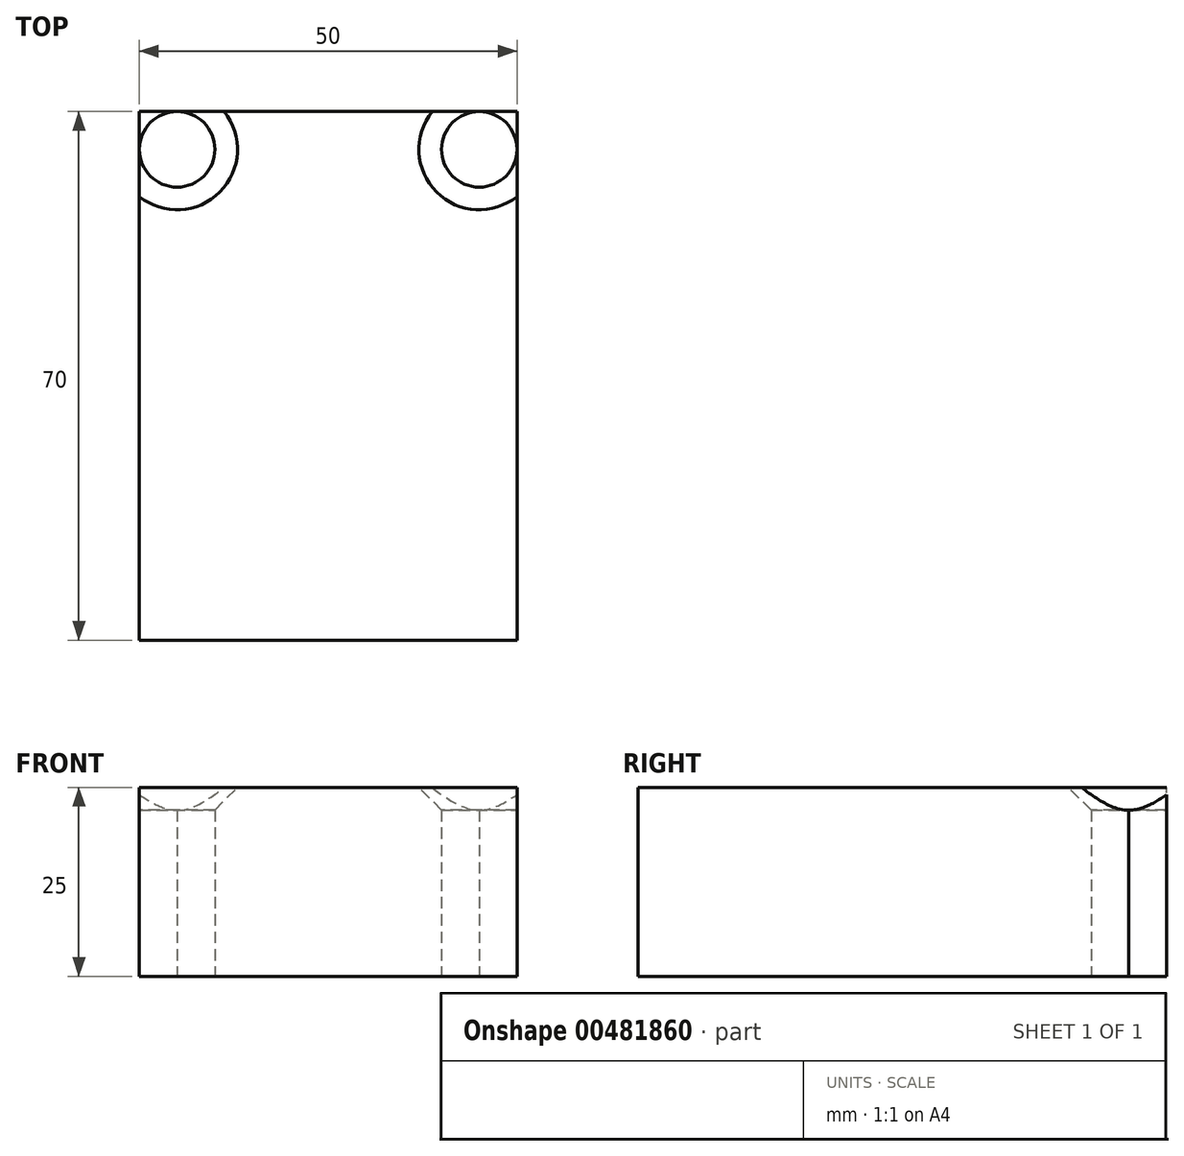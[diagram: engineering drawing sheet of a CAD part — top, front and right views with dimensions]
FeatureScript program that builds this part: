
annotation { "Feature Type Name" : "Feature", "Feature Type Description" : "" }
export const myFeature = defineFeature(function(context is Context, id is Id, definition is map)
    precondition{}
    {
        {
            var Q0;
            Q0=qCreatedBy(makeId("Top.planeOp"),FACE);
            var sketch = newSketch(context, id + "F0", { "sketchPlane" : qUnion([Q0])});
            skLineSegment(sketch, "E0.bottom", {"start": v(-25, 35) * mm, "end": v(25, 35) * mm});
            skLineSegment(sketch, "E0.top", {"start": v(-25, -35) * mm, "end": v(25, -35) * mm});
            skLineSegment(sketch, "E0.left", {"start": v(-25, 35) * mm, "end": v(-25, -35) * mm});
            skLineSegment(sketch, "E0.right", {"start": v(25, 35) * mm, "end": v(25, -35) * mm});
            skPoint(sketch, "E0.middle", {"position": v(0, 0) * mm});
            skCircle(sketch, "E1", {"center": v(-20, 30) * mm, "radius": 5 * mm});
            skCircle(sketch, "E2", {"center": v(20, 30) * mm, "radius": 5 * mm});
            skSolve(sketch);
        }
        {
            var Q0;
            Q0 = qSketchRegion(id + "F0", true);
            extrude(context, id + "F1", {"entities" : qUnion([Q0]), "depth" : 25 * mm});
        }
        {
            var Q0;
            {var subQ0=sQuery(id+"F0.wireOp",EDGE,"E1");var subQ1=makeQuery(id+"F0.imprint","INTERSECT",VERTEX,{"derivedFrom":[sQuery(id+"F0.wireOp",EDGE,"E0.bottom"),subQ0]});Q0=makeQuery(id+"F0.imprint","IMPRINT",FACE,{"disambiguationData":[TD([[makeQuery(id+"F0.imprint","IMPRINT",EDGE,{"disambiguationData":[TD([[subQ1,-1.0]])],"derivedFrom":subQ0}),1.0]])]});}
            var Q1;
            {var subQ0=sQuery(id+"F0.wireOp",EDGE,"E2");var subQ1=makeQuery(id+"F0.imprint","INTERSECT",VERTEX,{"derivedFrom":[sQuery(id+"F0.wireOp",EDGE,"E0.bottom"),subQ0]});Q1=makeQuery(id+"F0.imprint","IMPRINT",FACE,{"disambiguationData":[TD([[makeQuery(id+"F0.imprint","IMPRINT",EDGE,{"disambiguationData":[TD([[subQ1,1.0]])],"derivedFrom":subQ0}),1.0]])]});}
            extrude(context, id + "F2", {"entities" : qUnion([Q0, Q1]), "operationType" : NewBodyOperationType.REMOVE, "endBound" : BoundingType.THROUGH_ALL, "depth" : 25 * mm});
        }
        {
            var Q0;
            Q0=makeQuery(id+"F2.boolean.opBoolean","INTERSECT",EDGE,{"disambiguationData":[OD(0.0)],"derivedFrom":[makeQuery(id+"F1.opExtrude","CAP_FACE",FACE,{"disambiguationData":[OSD([sQuery(id+"F0.wireOp",EDGE,"E0.bottom"),sQuery(id+"F0.wireOp",EDGE,"E0.top"),sQuery(id+"F0.wireOp",EDGE,"E0.left"),sQuery(id+"F0.wireOp",EDGE,"E0.right")])],"isStart":false}),makeQuery(id+"F2.opExtrude","SWEPT_FACE",FACE,{"disambiguationData":[OSD([sQuery(id+"F0.wireOp",EDGE,"E1")])]})]});
            var Q1;
            Q1=makeQuery(id+"F2.boolean.opBoolean","INTERSECT",EDGE,{"disambiguationData":[OD(0.0)],"derivedFrom":[makeQuery(id+"F1.opExtrude","CAP_FACE",FACE,{"disambiguationData":[OSD([sQuery(id+"F0.wireOp",EDGE,"E0.bottom"),sQuery(id+"F0.wireOp",EDGE,"E0.top"),sQuery(id+"F0.wireOp",EDGE,"E0.left"),sQuery(id+"F0.wireOp",EDGE,"E0.right")])],"isStart":false}),makeQuery(id+"F2.opExtrude","SWEPT_FACE",FACE,{"disambiguationData":[OSD([sQuery(id+"F0.wireOp",EDGE,"E2")])]})]});
            chamfer(context, id + "F3", {"entities" : qUnion([Q0, Q1]), "width" : 3 * mm, "tangentPropagation" : true});
        }
        {
            var Q0;
            Q0=makeQuery(id+"F2.boolean.opBoolean","INTERSECT",EDGE,{"disambiguationData":[OD(1.0)],"derivedFrom":[makeQuery(id+"F1.opExtrude","CAP_FACE",FACE,{"disambiguationData":[OSD([sQuery(id+"F0.wireOp",EDGE,"E0.bottom"),sQuery(id+"F0.wireOp",EDGE,"E0.top"),sQuery(id+"F0.wireOp",EDGE,"E0.left"),sQuery(id+"F0.wireOp",EDGE,"E0.right")])],"isStart":false}),makeQuery(id+"F2.opExtrude","SWEPT_FACE",FACE,{"disambiguationData":[OSD([sQuery(id+"F0.wireOp",EDGE,"E2")])]})]});
            var Q1;
            Q1=makeQuery(id+"F2.boolean.opBoolean","INTERSECT",EDGE,{"disambiguationData":[OD(1.0)],"derivedFrom":[makeQuery(id+"F1.opExtrude","CAP_FACE",FACE,{"disambiguationData":[OSD([sQuery(id+"F0.wireOp",EDGE,"E0.bottom"),sQuery(id+"F0.wireOp",EDGE,"E0.top"),sQuery(id+"F0.wireOp",EDGE,"E0.left"),sQuery(id+"F0.wireOp",EDGE,"E0.right")])],"isStart":false}),makeQuery(id+"F2.opExtrude","SWEPT_FACE",FACE,{"disambiguationData":[OSD([sQuery(id+"F0.wireOp",EDGE,"E1")])]})]});
            chamfer(context, id + "F4", {"entities" : qUnion([Q0, Q1]), "width" : 3 * mm, "tangentPropagation" : true});
        }
    });
